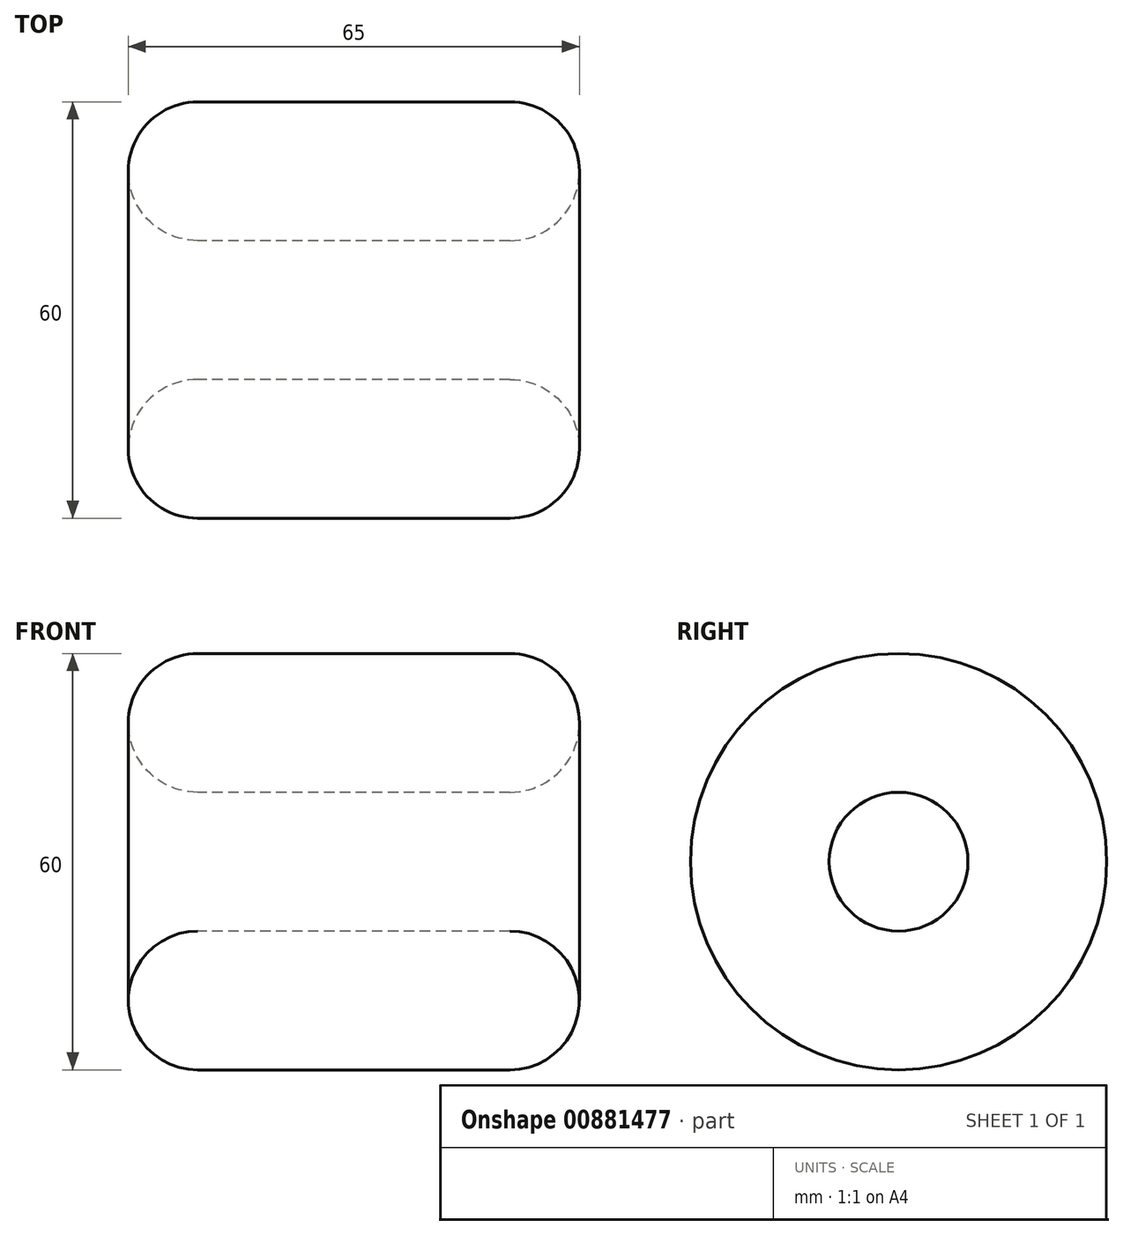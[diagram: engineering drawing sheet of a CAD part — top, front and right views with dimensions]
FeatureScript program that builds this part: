
annotation { "Feature Type Name" : "Feature", "Feature Type Description" : "" }
export const myFeature = defineFeature(function(context is Context, id is Id, definition is map)
    precondition{}
    {
        {
            var Q0;
            Q0=qCreatedBy(makeId("Right.planeOp"),FACE);
            var sketch = newSketch(context, id + "F0", { "sketchPlane" : qUnion([Q0])});
            skCircle(sketch, "E0", {"center": v(0, 0) * mm, "radius": 30 * mm});
            skCircle(sketch, "E1", {"center": v(0, 0) * mm, "radius": 10 * mm});
            skSolve(sketch);
        }
        {
            var Q0;
            Q0=makeQuery(id+"F0.imprint","IMPRINT",FACE,{"disambiguationData":[TD([[makeQuery(id+"F0.imprint","IMPRINT",EDGE,{"derivedFrom":sQuery(id+"F0.wireOp",EDGE,"E0")}),1.0]])]});
            extrude(context, id + "F1", {"entities" : qUnion([Q0]), "depth" : 65 * mm, "offsetDistance" : 25 * mm});
        }
        {
            var Q0;
            Q0=makeQuery(id+"F1.opExtrude","CAP_FACE",FACE,{"disambiguationData":[OSD([sQuery(id+"F0.wireOp",EDGE,"E0"),sQuery(id+"F0.wireOp",EDGE,"E1")])],"isStart":false});
            var Q1;
            Q1=makeQuery(id+"F1.opExtrude","SWEPT_FACE",FACE,{"disambiguationData":[OSD([sQuery(id+"F0.wireOp",EDGE,"E0")])]});
            var Q2;
            Q2=makeQuery(id+"F1.opExtrude","CAP_FACE",FACE,{"disambiguationData":[OSD([sQuery(id+"F0.wireOp",EDGE,"E0"),sQuery(id+"F0.wireOp",EDGE,"E1")])],"isStart":true});
            var Q3;
            Q3=makeQuery(id+"F1.opExtrude","SWEPT_FACE",FACE,{"disambiguationData":[OSD([sQuery(id+"F0.wireOp",EDGE,"E1")])]});
            fillet(context, id + "F2", {"entities" : qUnion([Q0, Q1, Q2, Q3]), "radius" : 10 * mm, "tangentPropagation" : true, "allowEdgeOverflow" : false});
        }
    });
